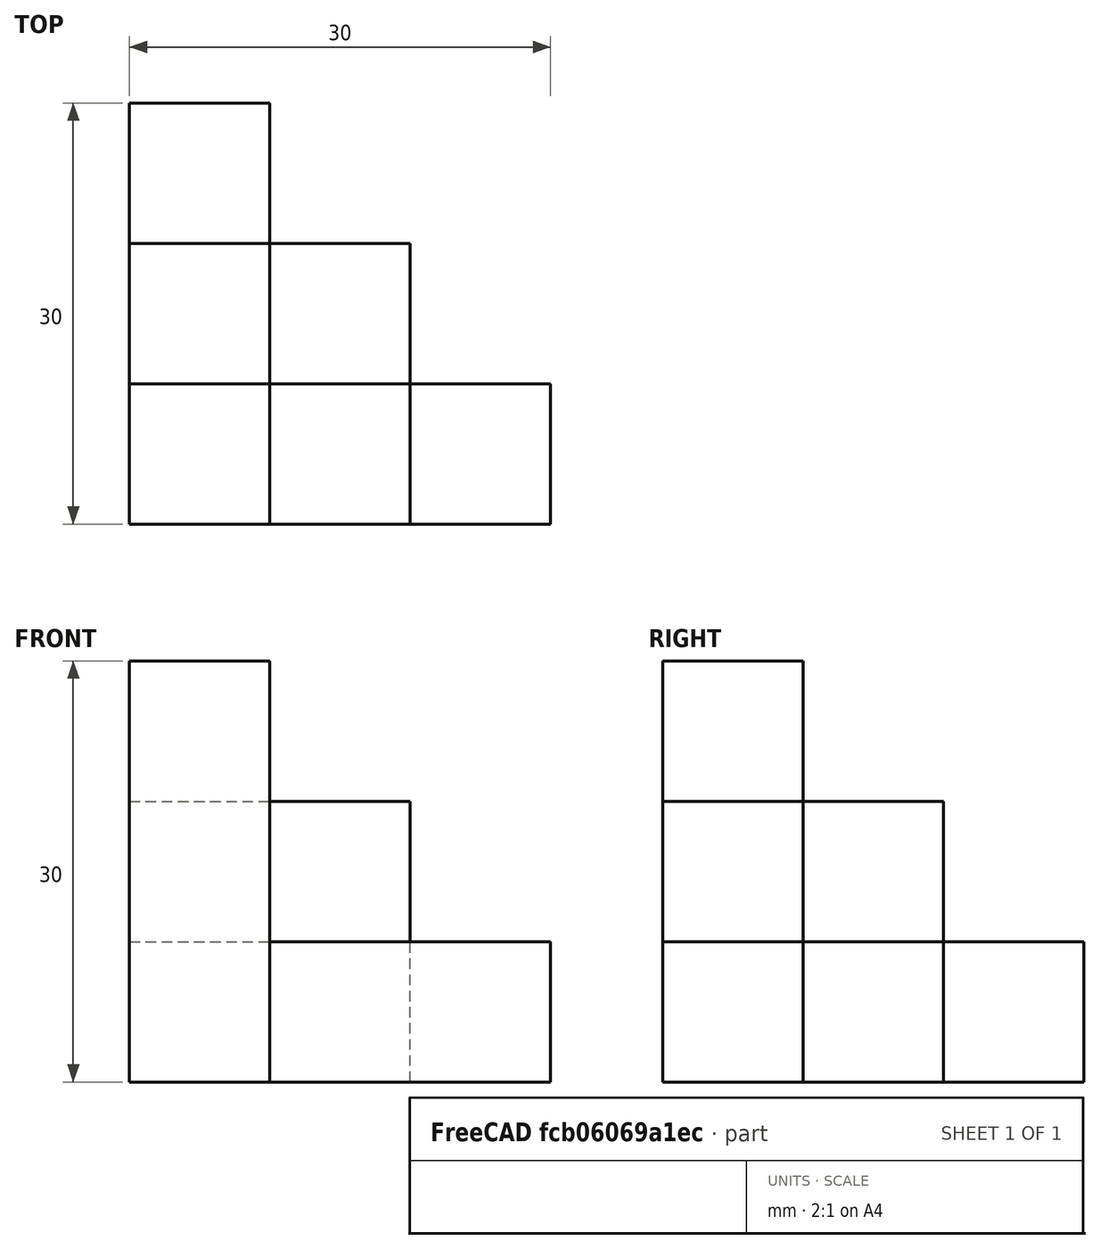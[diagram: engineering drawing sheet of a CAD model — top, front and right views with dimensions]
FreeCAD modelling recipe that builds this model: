
FCSTD DOCUMENT  (FreeCAD 1.0R39319 (Git))
Label: ojt1_t04r01_qbert 3 levels
License: All rights reserved
LicenseURL: https://en.wikipedia.org/wiki/All_rights_reserved
objects: Part::Box×6
note: 6 computed .brp shape members not serialized (recipe doc carries the construction recipe); baked Part::Feature solids carry a one-line shape summary decoded from their .brp

FEATURE [Part::Box] Box  label="Cub"
  AttacherType = Attacher::AttachEngine3D
  Height = 30
  Length = 10
  Width = 10
FEATURE [Part::Box] Box001  label="Cub001"
  AttacherType = Attacher::AttachEngine3D
  Height = 10
  Length = 20
  Placement = pos=(10,0,0) rot=(0,0,1;0rad)
  Width = 10
FEATURE [Part::Box] Box002  label="Cub002"
  AttacherType = Attacher::AttachEngine3D
  Height = 10
  Length = 10
  Placement = pos=(10,0,10) rot=(0,0,1;0rad)
  Width = 10
FEATURE [Part::Box] Box003  label="Cub003"
  AttacherType = Attacher::AttachEngine3D
  Height = 10
  Length = 10
  Placement = pos=(0,10,10) rot=(0,0,1;0rad)
  Width = 10
FEATURE [Part::Box] Box004  label="Cub004"
  AttacherType = Attacher::AttachEngine3D
  Height = 10
  Length = 10
  Placement = pos=(0,10,0) rot=(0.2,0,1.2;0rad)
  Width = 20
FEATURE [Part::Box] Box005  label="Cub005"
  AttacherType = Attacher::AttachEngine3D
  Height = 10
  Length = 10
  Placement = pos=(10,10,0) rot=(0,0,1;0rad)
  Width = 10
